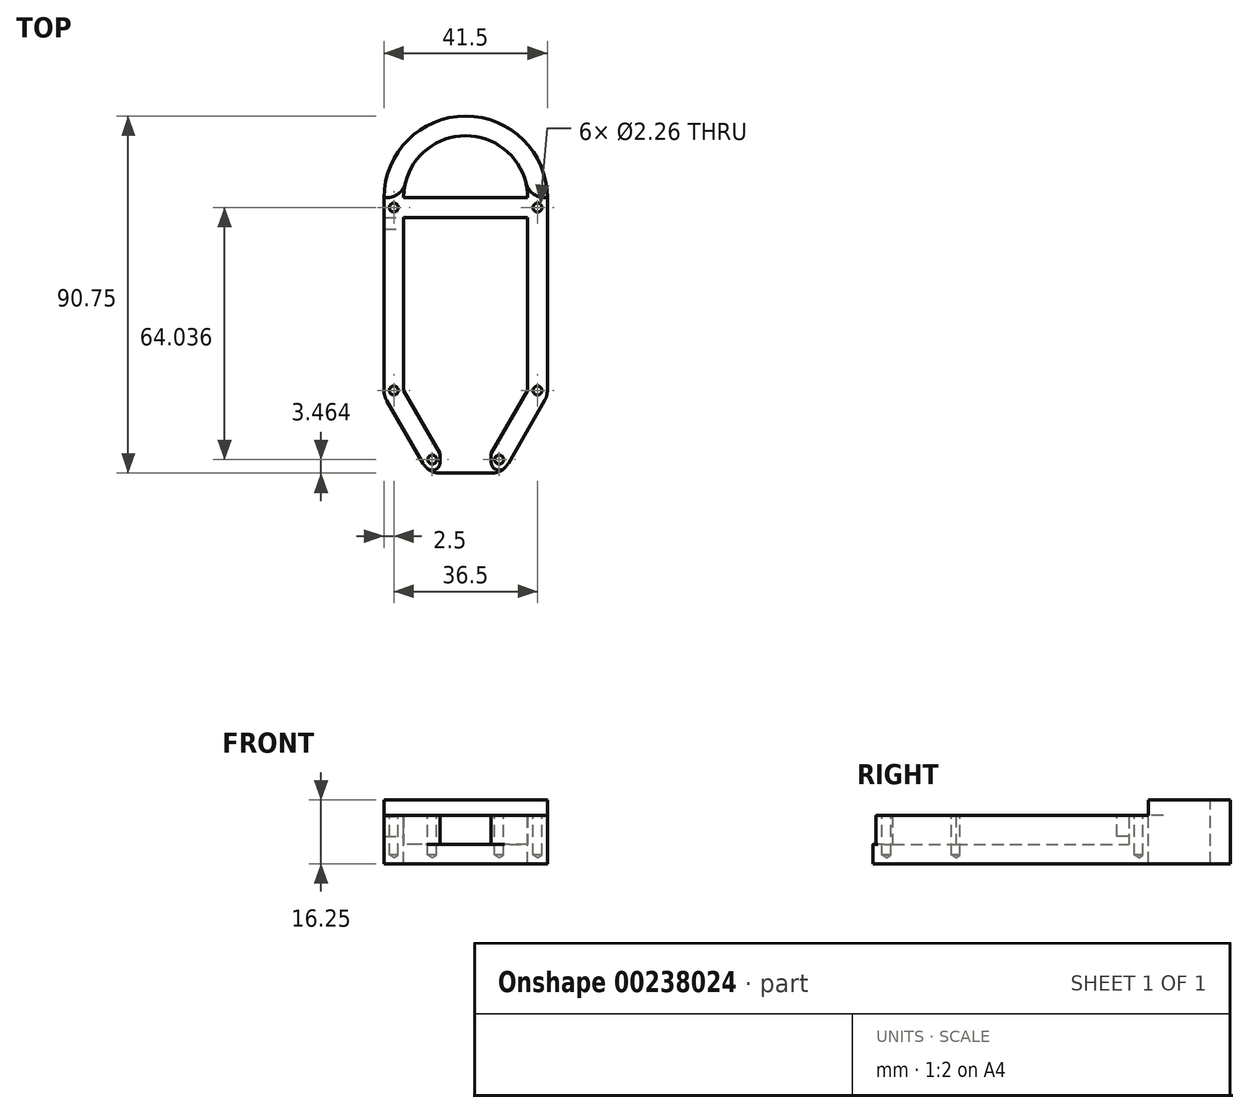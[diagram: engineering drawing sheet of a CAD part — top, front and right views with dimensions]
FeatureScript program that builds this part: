
annotation { "Feature Type Name" : "Feature", "Feature Type Description" : "" }
export const myFeature = defineFeature(function(context is Context, id is Id, definition is map)
    precondition{}
    {
        {
            var Q0;
            Q0=qCreatedBy(makeId("Top.planeOp"),FACE);
            var sketch = newSketch(context, id + "F0", { "sketchPlane" : qUnion([Q0])});
            skLineSegment(sketch, "E0", {"start": v(0, 0) * mm, "end": v(6.5, 0) * mm});
            skLineSegment(sketch, "E1", {"start": v(6.5, 0) * mm, "end": v(15.75, 16.02) * mm});
            skLineSegment(sketch, "E2", {"start": v(15.75, 16.02) * mm, "end": v(15.75, 60) * mm});
            skLineSegment(sketch, "E3", {"start": v(15.75, 60) * mm, "end": v(0, 60) * mm});
            skLineSegment(sketch, "E4.MirrorCS", {"start": v(-6.5, 0) * mm, "end": v(-15.75, 16.02) * mm});
            skLineSegment(sketch, "E5.MirrorCS", {"start": v(0, 0) * mm, "end": v(-6.5, 0) * mm});
            skLineSegment(sketch, "E6.MirrorCS", {"start": v(-15.75, 60) * mm, "end": v(0, 60) * mm});
            skLineSegment(sketch, "E7.MirrorCS", {"start": v(-15.75, 16.02) * mm, "end": v(-15.75, 60) * mm});
            skSolve(sketch);
        }
        {
            var Q0;
            Q0=makeQuery(id+"F0.imprint","IMPRINT",FACE,{"disambiguationData":[TD([[makeQuery(id+"F0.imprint","IMPRINT",EDGE,{"derivedFrom":sQuery(id+"F0.wireOp",EDGE,"E0")}),1.0]])]});
            extrude(context, id + "F1", {"entities" : qUnion([Q0]), "depth" : 7.25 * mm});
        }
        {
            var Q0;
            Q0=makeQuery(id+"F1.opExtrude","CAP_FACE",FACE,{"disambiguationData":[OSD([sQuery(id+"F0.wireOp",EDGE,"E0"),sQuery(id+"F0.wireOp",EDGE,"E1"),sQuery(id+"F0.wireOp",EDGE,"E2"),sQuery(id+"F0.wireOp",EDGE,"E3"),sQuery(id+"F0.wireOp",EDGE,"E4.MirrorCS"),sQuery(id+"F0.wireOp",EDGE,"E5.MirrorCS"),sQuery(id+"F0.wireOp",EDGE,"E6.MirrorCS"),sQuery(id+"F0.wireOp",EDGE,"E7.MirrorCS")])],"isStart":false});
            shell(context, id + "F2", {"entities" : qUnion([Q0]), "thickness" : 5 * mm, "oppositeDirection" : true});
        }
        {
            var Q0;
            Q0=makeQuery(id+"F2.opShell","OFFSET_FACE",FACE,{"disambiguationData":[OSD([sQuery(id+"F0.wireOp",EDGE,"E7.MirrorCS")])]});
            var sketch = newSketch(context, id + "F3", { "sketchPlane" : qUnion([Q0])});
            skLineSegment(sketch, "E8.bottom", {"start": v(60, 2) * mm, "end": v(57, 2) * mm});
            skLineSegment(sketch, "E8.top", {"start": v(60, 7) * mm, "end": v(57, 7) * mm});
            skLineSegment(sketch, "E8.left", {"start": v(60, 2) * mm, "end": v(60, 7) * mm});
            skLineSegment(sketch, "E8.right", {"start": v(57, 2) * mm, "end": v(57, 7) * mm});
            skSolve(sketch);
        }
        {
            var Q0;
            Q0 = qSketchRegion(id + "F3", true);
            extrude(context, id + "F4", {"entities" : qUnion([Q0]), "operationType" : NewBodyOperationType.REMOVE, "endBound" : BoundingType.UP_TO_NEXT, "oppositeDirection" : true, "depth" : 25.4 * mm});
        }
        {
            var Q0;
            Q0=makeQuery(id+"F1.opExtrude","CAP_FACE",FACE,{"disambiguationData":[OSD([sQuery(id+"F0.wireOp",EDGE,"E0"),sQuery(id+"F0.wireOp",EDGE,"E1"),sQuery(id+"F0.wireOp",EDGE,"E2"),sQuery(id+"F0.wireOp",EDGE,"E3"),sQuery(id+"F0.wireOp",EDGE,"E4.MirrorCS"),sQuery(id+"F0.wireOp",EDGE,"E5.MirrorCS"),sQuery(id+"F0.wireOp",EDGE,"E6.MirrorCS"),sQuery(id+"F0.wireOp",EDGE,"E7.MirrorCS")])],"isStart":false});
            var sketch = newSketch(context, id + "F5", { "sketchPlane" : qUnion([Q0])});
            skPoint(sketch, "E9", {"position": v(-18.25, 62.5) * mm});
            skPoint(sketch, "E10", {"position": v(18.25, 62.5) * mm});
            skPoint(sketch, "E11", {"position": v(-18.25, 16.02) * mm});
            skPoint(sketch, "E12", {"position": v(18.25, 16.02) * mm});
            skPoint(sketch, "E13.positionSnap0", {"position": v(0, 0) * mm});
            skPoint(sketch, "E14", {"position": v(-8.5, -1.54) * mm});
            skPoint(sketch, "E15", {"position": v(8.5, -1.54) * mm});
            skSolve(sketch);
        }
        {
            var Q0;
            Q0=sQuery(id+"F5.wireOp",VERTEX,"E9");
            var Q1;
            Q1=sQuery(id+"F5.wireOp",VERTEX,"E10");
            var Q2;
            Q2=sQuery(id+"F5.wireOp",VERTEX,"E11");
            var Q3;
            Q3=sQuery(id+"F5.wireOp",VERTEX,"E13");
            var Q4;
            Q4=sQuery(id+"F5.wireOp",VERTEX,"E12");
            var Q5;
            Q5=sQuery(id+"F5.wireOp",VERTEX,"E14");
            var Q6;
            Q6=sQuery(id+"F5.wireOp",VERTEX,"E15");
            var Q7;
            Q7=makeQuery(id+"F1.opExtrude","SWEPT_BODY",BODY,{"disambiguationData":[OSD([sQuery(id+"F0.wireOp",EDGE,"E0"),sQuery(id+"F0.wireOp",EDGE,"E1"),sQuery(id+"F0.wireOp",EDGE,"E2"),sQuery(id+"F0.wireOp",EDGE,"E3"),sQuery(id+"F0.wireOp",EDGE,"E4.MirrorCS"),sQuery(id+"F0.wireOp",EDGE,"E5.MirrorCS"),sQuery(id+"F0.wireOp",EDGE,"E6.MirrorCS"),sQuery(id+"F0.wireOp",EDGE,"E7.MirrorCS")])]});
            hole(context, id + "F6", {"style" : HoleStyle.SIMPLE, "endStyle" : HoleEndStyle.BLIND, "standardTappedOrClearance" : lookupTablePath({ "standard" : "ANSI", "engagement" : "75%", "pitch" : "40 tpi", "size" : "#4", "type" : "Tapped" }), "standardBlindInLast" : lookupTablePath({ "standard" : "ANSI", "engagement" : "75%", "pitch" : "40 tpi", "size" : "#4", "type" : "Tapped" }), "holeDiameter" : 2.26 * mm, "holeDepth" : 10 * mm, "locations" : qUnion([Q0, Q1, Q2, Q3, Q4, Q5, Q6]), "scope" : qUnion([Q7]), "showTappedDepth" : true, "tappedDepth" : 8.1 * mm, "tapClearance" : 3, "majorDiameter" : 2.84 * mm});
        }
        {
            var Q0;
            Q0=makeQuery(id+"F1.opExtrude","SWEPT_EDGE",EDGE,{"disambiguationData":[OSD([sQuery(id+"F0.wireOp",EDGE,"E4.MirrorCS"),sQuery(id+"F0.wireOp",EDGE,"E7.MirrorCS")])]});
            var Q1;
            Q1=makeQuery(id+"F1.opExtrude","SWEPT_EDGE",EDGE,{"disambiguationData":[OSD([sQuery(id+"F0.wireOp",EDGE,"E4.MirrorCS"),sQuery(id+"F0.wireOp",EDGE,"E5.MirrorCS")])]});
            var Q2;
            Q2=makeQuery(id+"F1.opExtrude","SWEPT_EDGE",EDGE,{"disambiguationData":[OSD([sQuery(id+"F0.wireOp",EDGE,"E0"),sQuery(id+"F0.wireOp",EDGE,"E1")])]});
            var Q3;
            Q3=makeQuery(id+"F1.opExtrude","SWEPT_EDGE",EDGE,{"disambiguationData":[OSD([sQuery(id+"F0.wireOp",EDGE,"E1"),sQuery(id+"F0.wireOp",EDGE,"E2")])]});
            fillet(context, id + "F7", {"entities" : qUnion([Q0, Q1, Q2, Q3]), "radius" : 5 * mm, "tangentPropagation" : true, "allowEdgeOverflow" : false});
        }
        {
            var Q0;
            Q0=makeQuery(id+"F1.opExtrude","CAP_FACE",FACE,{"disambiguationData":[OSD([sQuery(id+"F0.wireOp",EDGE,"E0"),sQuery(id+"F0.wireOp",EDGE,"E1"),sQuery(id+"F0.wireOp",EDGE,"E2"),sQuery(id+"F0.wireOp",EDGE,"E3"),sQuery(id+"F0.wireOp",EDGE,"E4.MirrorCS"),sQuery(id+"F0.wireOp",EDGE,"E5.MirrorCS"),sQuery(id+"F0.wireOp",EDGE,"E6.MirrorCS"),sQuery(id+"F0.wireOp",EDGE,"E7.MirrorCS")])],"isStart":false});
            var sketch = newSketch(context, id + "F8", { "sketchPlane" : qUnion([Q0])});
            skLineSegment(sketch, "E16.bottom", {"start": v(-6.5, 0) * mm, "end": v(6.5, 0) * mm});
            skLineSegment(sketch, "E16.top", {"start": v(-6.5, -5) * mm, "end": v(6.5, -5) * mm});
            skLineSegment(sketch, "E16.left", {"start": v(-6.5, 0) * mm, "end": v(-6.5, -5) * mm});
            skLineSegment(sketch, "E16.right", {"start": v(6.5, 0) * mm, "end": v(6.5, -5) * mm});
            skSolve(sketch);
        }
        {
            var Q0;
            Q0=makeQuery(id+"F8.imprint","IMPRINT",FACE,{"disambiguationData":[TD([[makeQuery(id+"F8.imprint","IMPRINT",EDGE,{"derivedFrom":sQuery(id+"F8.wireOp",EDGE,"E16.bottom")}),1.0]])]});
            var Q1;
            Q1=makeQuery(id+"F2.opShell","OFFSET_FACE",FACE,{"disambiguationData":[OSD([sQuery(id+"F0.wireOp",EDGE,"E0"),sQuery(id+"F0.wireOp",EDGE,"E1"),sQuery(id+"F0.wireOp",EDGE,"E2"),sQuery(id+"F0.wireOp",EDGE,"E3"),sQuery(id+"F0.wireOp",EDGE,"E4.MirrorCS"),sQuery(id+"F0.wireOp",EDGE,"E5.MirrorCS"),sQuery(id+"F0.wireOp",EDGE,"E6.MirrorCS"),sQuery(id+"F0.wireOp",EDGE,"E7.MirrorCS")])]});
            extrude(context, id + "F9", {"entities" : qUnion([Q0]), "operationType" : NewBodyOperationType.REMOVE, "endBound" : BoundingType.UP_TO_SURFACE, "oppositeDirection" : true, "endBoundEntityFace" : qUnion([Q1]), "depth" : 25 * mm});
        }
        {
            var Q0;
            {var subQ0=sQuery(id+"F0.wireOp",EDGE,"E5.MirrorCS");var subQ1=sQuery(id+"F0.wireOp",EDGE,"E4.MirrorCS");var subQ2=sQuery(id+"F0.wireOp",EDGE,"E0");Q0=makeQuery(id+"F9.boolean.opBoolean","MERGE",EDGE,{"derivedFrom":[makeQuery(id+"F7.opFillet","BLEND_EDGE",EDGE,{"blendedFrom":[makeQuery(id+"F1.opExtrude","SWEPT_EDGE",EDGE,{"disambiguationData":[OSD([subQ1,subQ0])]}),makeQuery(id+"F1.opExtrude","SWEPT_FACE",FACE,{"disambiguationData":[OSD([subQ2,subQ0])]})],"blendedInto":[makeQuery(id+"F1.opExtrude","SWEPT_FACE",FACE,{"disambiguationData":[OSD([subQ2,subQ0])]})]}),makeQuery(id+"F9.opExtrude","SWEPT_EDGE",EDGE,{"disambiguationData":[OSD([subQ2,sQuery(id+"F0.wireOp",EDGE,"E1"),sQuery(id+"F0.wireOp",EDGE,"E2"),sQuery(id+"F0.wireOp",EDGE,"E3"),subQ1,subQ0,sQuery(id+"F0.wireOp",EDGE,"E6.MirrorCS"),sQuery(id+"F0.wireOp",EDGE,"E7.MirrorCS"),sQuery(id+"F8.wireOp",EDGE,"E16.top"),sQuery(id+"F8.wireOp",EDGE,"E16.left")])]})]});}
            var Q1;
            {var subQ0=sQuery(id+"F0.wireOp",EDGE,"E5.MirrorCS");var subQ1=sQuery(id+"F0.wireOp",EDGE,"E1");var subQ2=sQuery(id+"F0.wireOp",EDGE,"E0");Q1=makeQuery(id+"F9.boolean.opBoolean","MERGE",EDGE,{"derivedFrom":[makeQuery(id+"F7.opFillet","BLEND_EDGE",EDGE,{"blendedFrom":[makeQuery(id+"F1.opExtrude","SWEPT_EDGE",EDGE,{"disambiguationData":[OSD([subQ2,subQ1])]}),makeQuery(id+"F1.opExtrude","SWEPT_FACE",FACE,{"disambiguationData":[OSD([subQ2,subQ0])]})],"blendedInto":[makeQuery(id+"F1.opExtrude","SWEPT_FACE",FACE,{"disambiguationData":[OSD([subQ2,subQ0])]})]}),makeQuery(id+"F9.opExtrude","SWEPT_EDGE",EDGE,{"disambiguationData":[OSD([subQ2,subQ1,sQuery(id+"F0.wireOp",EDGE,"E2"),sQuery(id+"F0.wireOp",EDGE,"E3"),sQuery(id+"F0.wireOp",EDGE,"E4.MirrorCS"),subQ0,sQuery(id+"F0.wireOp",EDGE,"E6.MirrorCS"),sQuery(id+"F0.wireOp",EDGE,"E7.MirrorCS"),sQuery(id+"F8.wireOp",EDGE,"E16.top"),sQuery(id+"F8.wireOp",EDGE,"E16.right")])]})]});}
            fillet(context, id + "F10", {"entities" : qUnion([Q0, Q1]), "radius" : 2 * mm, "tangentPropagation" : true, "allowEdgeOverflow" : false});
        }
        {
            var Q0;
            Q0=qCreatedBy(makeId("Top.planeOp"),FACE);
            var Q1;
            Q1=qCreatedBy(makeId("Top.planeOp"),FACE);
            var sketch = newSketch(context, id + "F11", { "sketchPlane" : qUnion([Q0, Q1])});
            skPoint(sketch, "E17.0", {"position": v(-20.75, 65) * mm});
            skPoint(sketch, "E18.0", {"position": v(20.75, 65) * mm});
            skArc(sketch, "E19", {"start": v(20.75, 65) * mm, "mid": v(0, 85.75) * mm, "end": v(-20.75, 65) * mm});
            skSolve(sketch);
        }
        {
            var Q0;
            Q0=makeQuery(id+"F1.opExtrude","SWEPT_FACE",FACE,{"disambiguationData":[OSD([sQuery(id+"F0.wireOp",EDGE,"E3"),sQuery(id+"F0.wireOp",EDGE,"E6.MirrorCS")])]});
            var sketch = newSketch(context, id + "F12", { "sketchPlane" : qUnion([Q0])});
            skLineSegment(sketch, "E20.0", {"start": v(-20.75, -5) * mm, "end": v(20.75, -5) * mm});
            skLineSegment(sketch, "E21.0", {"start": v(-20.75, 7.25) * mm, "end": v(-20.75, -5) * mm});
            skLineSegment(sketch, "E22.0", {"start": v(20.75, 7.25) * mm, "end": v(20.75, -5) * mm});
            skLineSegment(sketch, "E23.bottom", {"start": v(-20.75, -5) * mm, "end": v(-15.75, -5) * mm});
            skLineSegment(sketch, "E23.top", {"start": v(-20.75, 11.25) * mm, "end": v(-15.75, 11.25) * mm});
            skLineSegment(sketch, "E23.left", {"start": v(-20.75, -5) * mm, "end": v(-20.75, 11.25) * mm});
            skLineSegment(sketch, "E23.right", {"start": v(-15.75, -5) * mm, "end": v(-15.75, 11.25) * mm});
            skSolve(sketch);
        }
        {
            var Q0;
            Q0 = qSketchRegion(id + "F12", true);
            var Q1;
            Q1 = qConstructionFilter(qBodyType(qCreatedBy(id + "F11" ,EDGE), BodyType.WIRE), ConstructionObject.NO);
            sweep(context, id + "F13", {"operationType" : NewBodyOperationType.ADD, "profiles" : qUnion([Q0]), "path" : qUnion([Q1])});
        }
        {
            var Q0;
            {var subQ0=sQuery(id+"F12.wireOp",EDGE,"E23.right");var subQ1=sQuery(id+"F12.wireOp",EDGE,"E23.bottom");var subQ2=sQuery(id+"F11.wireOp",VERTEX,"E19.start");var subQ11=sQuery(id+"F11.wireOp",EDGE,"E19");Q0=makeQuery(id+"F13.boolean.opBoolean","SPLIT",EDGE,{"disambiguationData":[TD([makeQuery(id+"F13.opSweep","SWEPT_FACE",FACE,{"disambiguationData":[OSD([subQ11,subQ1])]})])],"derivedFrom":makeQuery(id+"F13.opSweep","CAP_EDGE",EDGE,{"disambiguationData":[OSD([subQ2,subQ0])],"isStart":true})});}
            fillet(context, id + "F14", {"entities" : qUnion([Q0]), "radius" : 5 * mm, "tangentPropagation" : true, "allowEdgeOverflow" : false});
        }
        {
            var Q0;
            {var subQ0=sQuery(id+"F12.wireOp",EDGE,"E23.right");var subQ1=sQuery(id+"F12.wireOp",EDGE,"E23.bottom");var subQ2=sQuery(id+"F11.wireOp",VERTEX,"E19.end");var subQ11=sQuery(id+"F11.wireOp",EDGE,"E19");Q0=makeQuery(id+"F13.boolean.opBoolean","SPLIT",EDGE,{"disambiguationData":[TD([makeQuery(id+"F13.opSweep","SWEPT_FACE",FACE,{"disambiguationData":[OSD([subQ11,subQ1])]})])],"derivedFrom":makeQuery(id+"F13.opSweep","CAP_EDGE",EDGE,{"disambiguationData":[OSD([subQ2,subQ0])],"isStart":false})});}
            fillet(context, id + "F15", {"entities" : qUnion([Q0]), "radius" : 5 * mm, "tangentPropagation" : true, "allowEdgeOverflow" : false});
        }
    });
